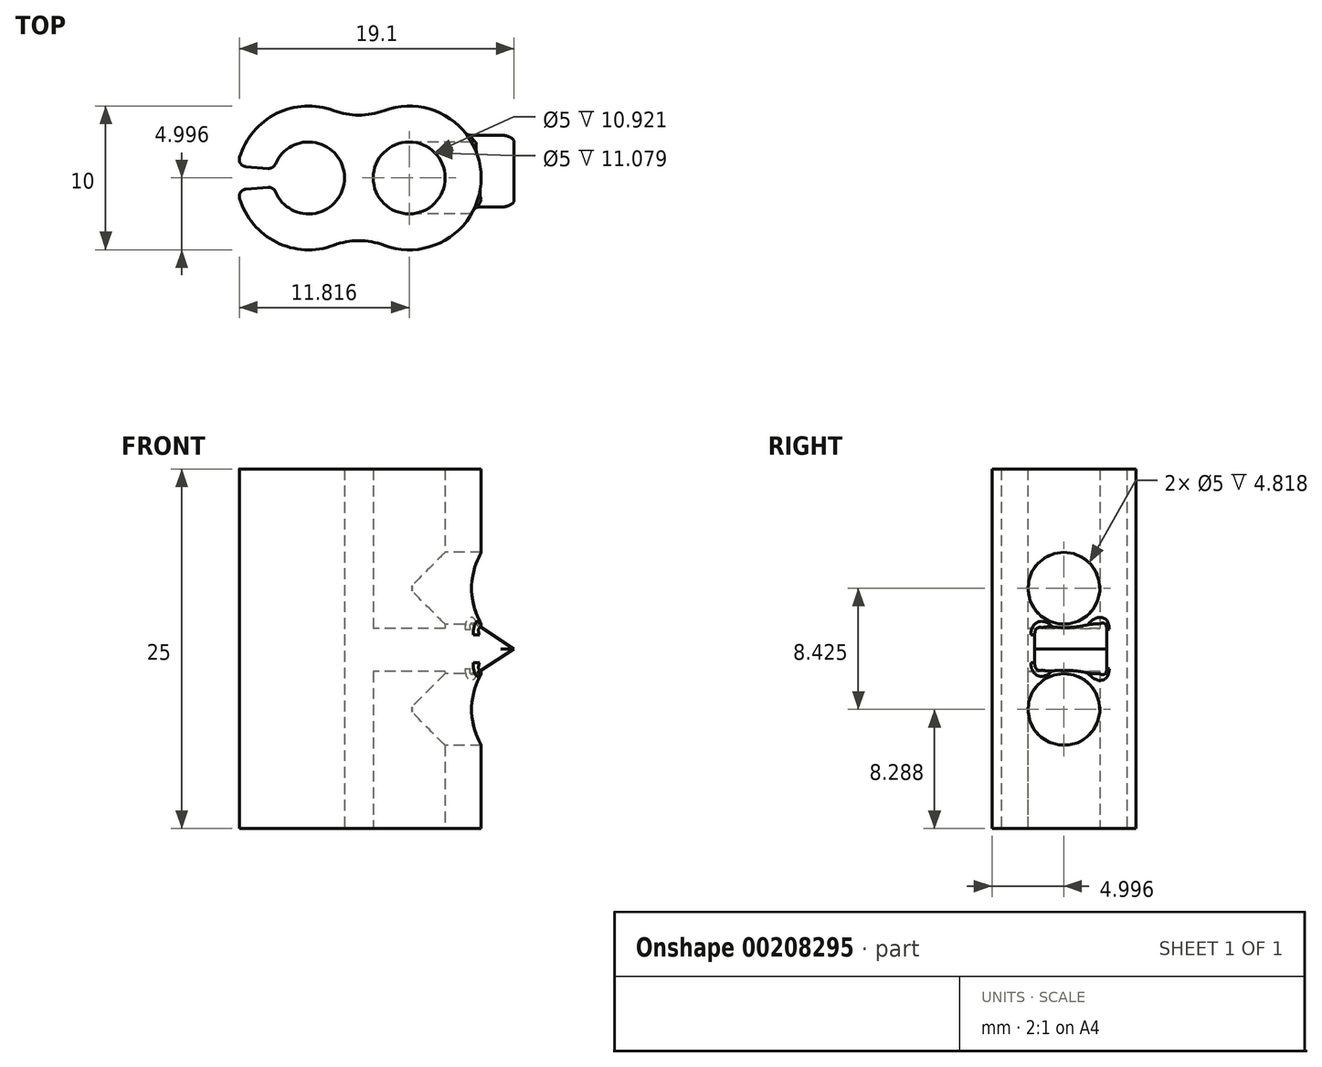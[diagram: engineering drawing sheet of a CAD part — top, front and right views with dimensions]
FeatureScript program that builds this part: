
annotation { "Feature Type Name" : "Feature", "Feature Type Description" : "" }
export const myFeature = defineFeature(function(context is Context, id is Id, definition is map)
    precondition{}
    {
        {
            var Q0;
            Q0=qCreatedBy(makeId("Top.planeOp"),FACE);
            var sketch = newSketch(context, id + "F0", { "sketchPlane" : qUnion([Q0])});
            skArc(sketch, "E0", {"start": v(-6.52, -1.44) * mm, "mid": v(-1.71, -0.47) * mm, "end": v(-6.52, 0.49) * mm});
            skLineSegment(sketch, "E1", {"start": v(-4.21, -0.47) * mm, "end": v(2.79, -0.47) * mm, "construction": true});
            skPoint(sketch, "E2", {"position": v(-0.71, -0.47) * mm});
            skArc(sketch, "E3", {"start": v(-2.46, 4.2) * mm, "mid": v(-6.44, 4) * mm, "end": v(-9, 0.95) * mm});
            skArc(sketch, "E4", {"start": v(1.04, -5.16) * mm, "mid": v(7.79, -0.47) * mm, "end": v(1.04, 4.2) * mm});
            skPoint(sketch, "E5.visualSharp", {"position": v(-0.71, 3.1) * mm});
            skArc(sketch, "E5.filletArc", {"start": v(-2.46, 4.2) * mm, "mid": v(-0.71, 3.9) * mm, "end": v(1.04, 4.2) * mm});
            skPoint(sketch, "E6.visualSharp", {"position": v(-0.71, -4.04) * mm});
            skArc(sketch, "E6.filletArc", {"start": v(1.04, -5.16) * mm, "mid": v(-0.71, -4.84) * mm, "end": v(-2.46, -5.16) * mm});
            skArc(sketch, "E7.trimOffspring", {"start": v(-9, -1.9) * mm, "mid": v(-6.44, -4.95) * mm, "end": v(-2.46, -5.16) * mm});
            skLineSegment(sketch, "E8", {"start": v(-8.57, 0.31) * mm, "end": v(-7.02, 0.18) * mm});
            skLineSegment(sketch, "E9", {"start": v(-8.57, -1.26) * mm, "end": v(-7.02, -1.13) * mm});
            skPoint(sketch, "E10.visualSharp", {"position": v(-6.63, -1.1) * mm});
            skArc(sketch, "E10.filletArc", {"start": v(-6.52, -1.44) * mm, "mid": v(-6.72, -1.2) * mm, "end": v(-7.02, -1.13) * mm});
            skPoint(sketch, "E11.visualSharp", {"position": v(-6.63, 0.15) * mm});
            skArc(sketch, "E11.filletArc", {"start": v(-7.02, 0.18) * mm, "mid": v(-6.72, 0.25) * mm, "end": v(-6.52, 0.49) * mm});
            skPoint(sketch, "E12.visualSharp", {"position": v(-9.14, -1.3) * mm});
            skArc(sketch, "E12.filletArc", {"start": v(-8.57, -1.26) * mm, "mid": v(-8.94, -1.48) * mm, "end": v(-9, -1.9) * mm});
            skPoint(sketch, "E13.visualSharp", {"position": v(-9.14, 0.36) * mm});
            skArc(sketch, "E13.filletArc", {"start": v(-9, 0.95) * mm, "mid": v(-8.94, 0.53) * mm, "end": v(-8.57, 0.31) * mm});
            skCircle(sketch, "E14", {"center": v(2.79, -0.47) * mm, "radius": 2.5 * mm});
            skSolve(sketch);
        }
        {
            var Q0;
            Q0=qCreatedBy(makeId("Front.planeOp"),FACE);
            var sketch = newSketch(context, id + "F1", { "sketchPlane" : qUnion([Q0])});
            skFitSpline(sketch, "E15.0", {"points": [v(7.79, 19.21) * mm, v(7.79, 19.21) * mm, v(7.72, 19.08) * mm, v(7.53, 18.66) * mm, v(7.4, 18.3) * mm, v(7.31, 18.04) * mm, v(7.22, 17.69) * mm, v(7.14, 17.2) * mm, v(7.11, 16.8) * mm, v(7.12, 16.46) * mm, v(7.14, 16.22) * mm, v(7.18, 15.98) * mm, v(7.24, 15.67) * mm, v(7.33, 15.3) * mm, v(7.46, 14.93) * mm, v(7.6, 14.63) * mm, v(7.73, 14.31) * mm, v(7.79, 14.21) * mm, v(7.79, 14.21) * mm], "construction": true});
            skFitSpline(sketch, "E16.0", {"points": [v(7.79, 10.79) * mm, v(7.79, 10.79) * mm, v(7.72, 10.65) * mm, v(7.53, 10.23) * mm, v(7.4, 9.88) * mm, v(7.31, 9.62) * mm, v(7.22, 9.26) * mm, v(7.14, 8.78) * mm, v(7.11, 8.37) * mm, v(7.12, 8.04) * mm, v(7.14, 7.8) * mm, v(7.18, 7.55) * mm, v(7.24, 7.24) * mm, v(7.33, 6.89) * mm, v(7.46, 6.5) * mm, v(7.6, 6.2) * mm, v(7.73, 5.89) * mm, v(7.79, 5.79) * mm, v(7.79, 5.79) * mm], "construction": true});
            skLineSegment(sketch, "E17", {"start": v(11.22, 12.5) * mm, "end": v(5.45, 12.5) * mm, "construction": true});
            skLineSegment(sketch, "E18", {"start": v(5.45, 15.5) * mm, "end": v(10.07, 12.5) * mm});
            skLineSegment(sketch, "E19", {"start": v(10.07, 12.5) * mm, "end": v(5.45, 9.5) * mm});
            skLineSegment(sketch, "E20", {"start": v(5.45, 9.5) * mm, "end": v(5.45, 15.5) * mm});
            skSolve(sketch);
        }
        {
            var Q0;
            Q0 = qSketchRegion(id + "F0", true);
            extrude(context, id + "F2", {"entities" : qUnion([Q0]), "depth" : 25 * mm});
        }
        {
            var Q0;
            Q0 = qSketchRegion(id + "F1", true);
            extrude(context, id + "F3", {"entities" : qUnion([Q0]), "operationType" : NewBodyOperationType.ADD, "endBound" : BoundingType.SYMMETRIC, "depth" : 5 * mm});
        }
        {
            var Q0;
            Q0=makeQuery(id+"F3.opExtrude","CAP_FACE",FACE,{"disambiguationData":[OSD([sQuery(id+"F1.wireOp",EDGE,"E18"),sQuery(id+"F1.wireOp",EDGE,"E19"),sQuery(id+"F1.wireOp",EDGE,"E20")])],"isStart":false});
            var Q1;
            Q1=makeQuery(id+"F3.opExtrude","CAP_FACE",FACE,{"disambiguationData":[OSD([sQuery(id+"F1.wireOp",EDGE,"E18"),sQuery(id+"F1.wireOp",EDGE,"E19"),sQuery(id+"F1.wireOp",EDGE,"E20")])],"isStart":true});
            fillet(context, id + "F4", {"entities" : qUnion([Q0, Q1]), "radius" : 0.5 * mm, "tangentPropagation" : true, "allowEdgeOverflow" : false});
        }
        {
            var Q0;
            Q0=qCreatedBy(makeId("Right.planeOp"),FACE);
            var sketch = newSketch(context, id + "F5", { "sketchPlane" : qUnion([Q0])});
            skCircle(sketch, "E21", {"center": v(-0.47, 16.71) * mm, "radius": 2.5 * mm});
            skCircle(sketch, "E22", {"center": v(-0.47, 8.29) * mm, "radius": 2.5 * mm});
            skLineSegment(sketch, "E23.0", {"start": v(-5.47, 25) * mm, "end": v(4.53, 25) * mm, "construction": true});
            skPoint(sketch, "E24", {"position": v(-0.47, 25) * mm});
            skLineSegment(sketch, "E25", {"start": v(-0.47, 25) * mm, "end": v(-0.47, 1.44) * mm, "construction": true});
            skSolve(sketch);
        }
        {
            var Q0;
            Q0 = qSketchRegion(id + "F5", true);
            extrude(context, id + "F6", {"entities" : qUnion([Q0]), "operationType" : NewBodyOperationType.REMOVE, "depth" : 10.9 * mm, "hasSecondDirection" : true, "secondDirectionOppositeDirection" : false, "secondDirectionDepth" : 2.97 * mm});
        }
        {
            var Q0;
            Q0=qCreatedBy(makeId("Right.planeOp"),FACE);
            var sketch = newSketch(context, id + "F7", { "sketchPlane" : qUnion([Q0])});
            skLineSegment(sketch, "E26", {"start": v(4.52, 25) * mm, "end": v(4.52, 0) * mm, "construction": true});
            skLineSegment(sketch, "E27", {"start": v(-4.47, 0) * mm, "end": v(-4.47, 25) * mm, "construction": true});
            skLineSegment(sketch, "E28.bottom", {"start": v(-4.48, 10.92) * mm, "end": v(3.52, 10.92) * mm});
            skLineSegment(sketch, "E28.top", {"start": v(-4.48, 13.92) * mm, "end": v(3.52, 13.92) * mm});
            skLineSegment(sketch, "E28.left", {"start": v(-4.48, 10.92) * mm, "end": v(-4.48, 13.92) * mm});
            skLineSegment(sketch, "E28.right", {"start": v(3.52, 10.92) * mm, "end": v(3.52, 13.92) * mm});
            skSolve(sketch);
        }
        {
            var Q0;
            Q0 = qSketchRegion(id + "F7", true);
            extrude(context, id + "F8", {"entities" : qUnion([Q0]), "operationType" : NewBodyOperationType.ADD, "depth" : 5.7 * mm});
        }
    });
